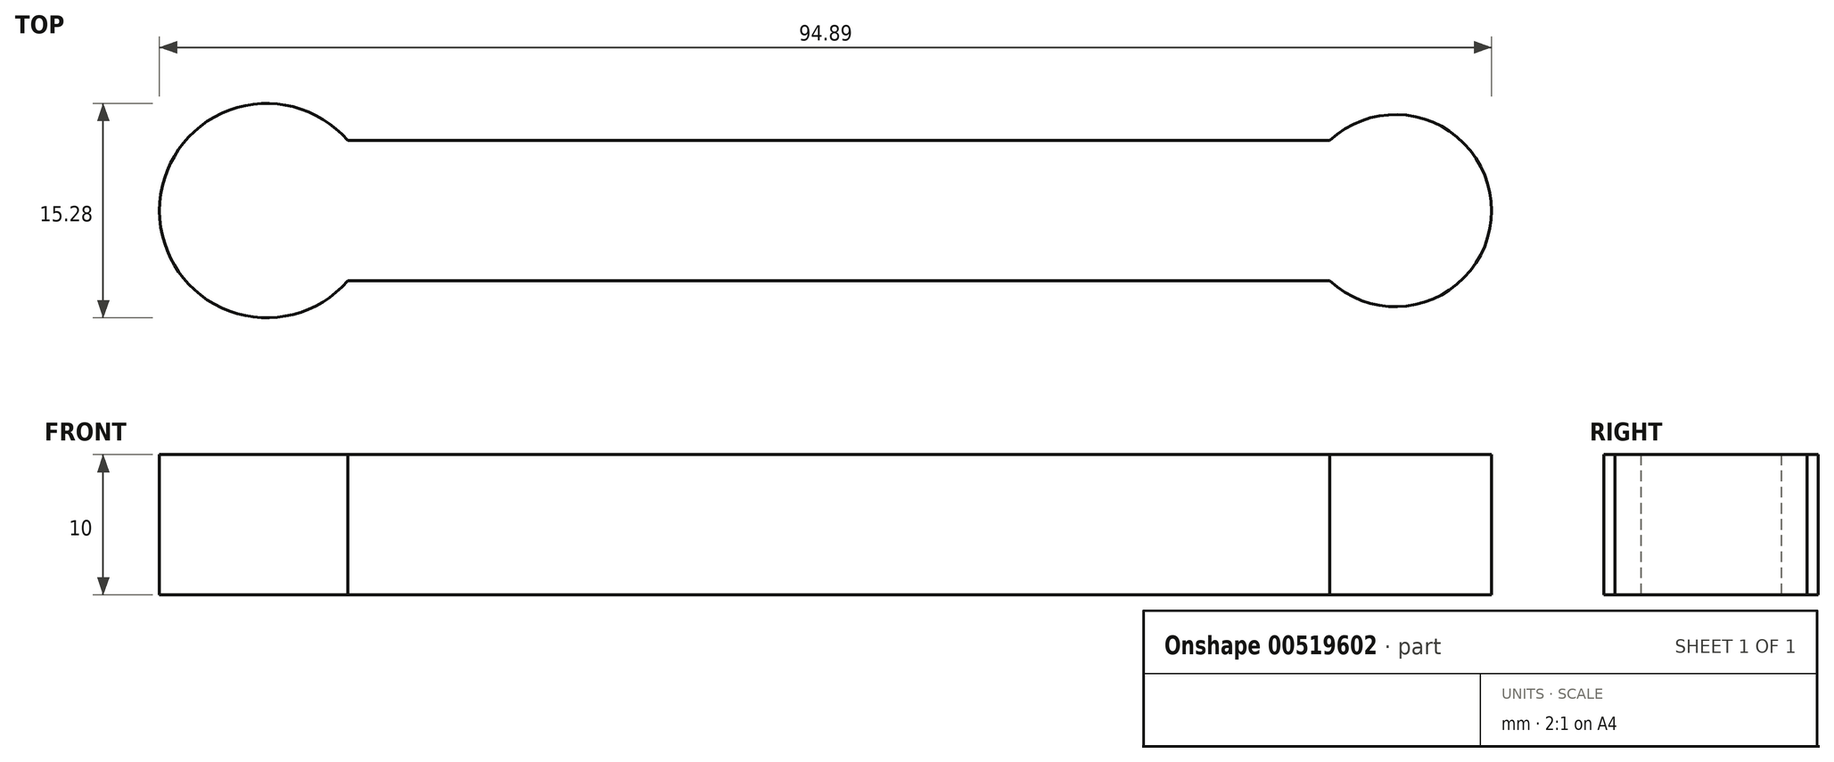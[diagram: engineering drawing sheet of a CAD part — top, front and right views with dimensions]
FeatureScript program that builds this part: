
annotation { "Feature Type Name" : "Feature", "Feature Type Description" : "" }
export const myFeature = defineFeature(function(context is Context, id is Id, definition is map)
    precondition{}
    {
        {
            var Q0;
            Q0=qCreatedBy(makeId("Top.planeOp"),FACE);
            var sketch = newSketch(context, id + "F0", { "sketchPlane" : qUnion([Q0])});
            skCircle(sketch, "E0", {"center": v(-92, 55.87) * mm, "radius": 12.7 * mm});
            skSolve(sketch);
        }
        {
            var Q0;
            Q0=qCreatedBy(makeId("Top.planeOp"),FACE);
            var sketch = newSketch(context, id + "F1", { "sketchPlane" : qUnion([Q0])});
            skCircle(sketch, "E1", {"center": v(-236.94, -25.35) * mm, "radius": 5 * mm});
            skSolve(sketch);
        }
        {
            var Q0;
            Q0=makeQuery(id+"F1.imprint","IMPRINT",FACE,{"disambiguationData":[TD([[makeQuery(id+"F1.imprint","IMPRINT",EDGE,{"derivedFrom":sQuery(id+"F1.wireOp",EDGE,"E1")}),1.0]])]});
            var sketch = newSketch(context, id + "F2", { "sketchPlane" : qUnion([Q0])});
            skLineSegment(sketch, "E2.bottom", {"start": v(-209.03, -142.51) * mm, "end": v(-139.03, -142.51) * mm});
            skLineSegment(sketch, "E2.top", {"start": v(-209.03, -152.51) * mm, "end": v(-139.03, -152.51) * mm});
            skLineSegment(sketch, "E2.left", {"start": v(-209.03, -142.51) * mm, "end": v(-209.03, -152.51) * mm});
            skLineSegment(sketch, "E2.right", {"start": v(-139.03, -142.51) * mm, "end": v(-139.03, -152.51) * mm});
            skCircle(sketch, "E3", {"center": v(-134.4, -147.51) * mm, "radius": 6.85 * mm});
            skPoint(sketch, "E3.centerSnap0", {"position": v(-139.03, -147.51) * mm});
            skCircle(sketch, "E4", {"center": v(-214.8, -147.51) * mm, "radius": 7.64 * mm});
            skPoint(sketch, "E4.centerSnap0", {"position": v(-209.03, -147.51) * mm});
            skSolve(sketch);
        }
        {
            var Q0;
            Q0 = qSketchRegion(id + "F2", true);
            extrude(context, id + "F3", {"entities" : qUnion([Q0]), "depth" : 10 * mm, "offsetDistance" : 25.4 * mm});
        }
    });
